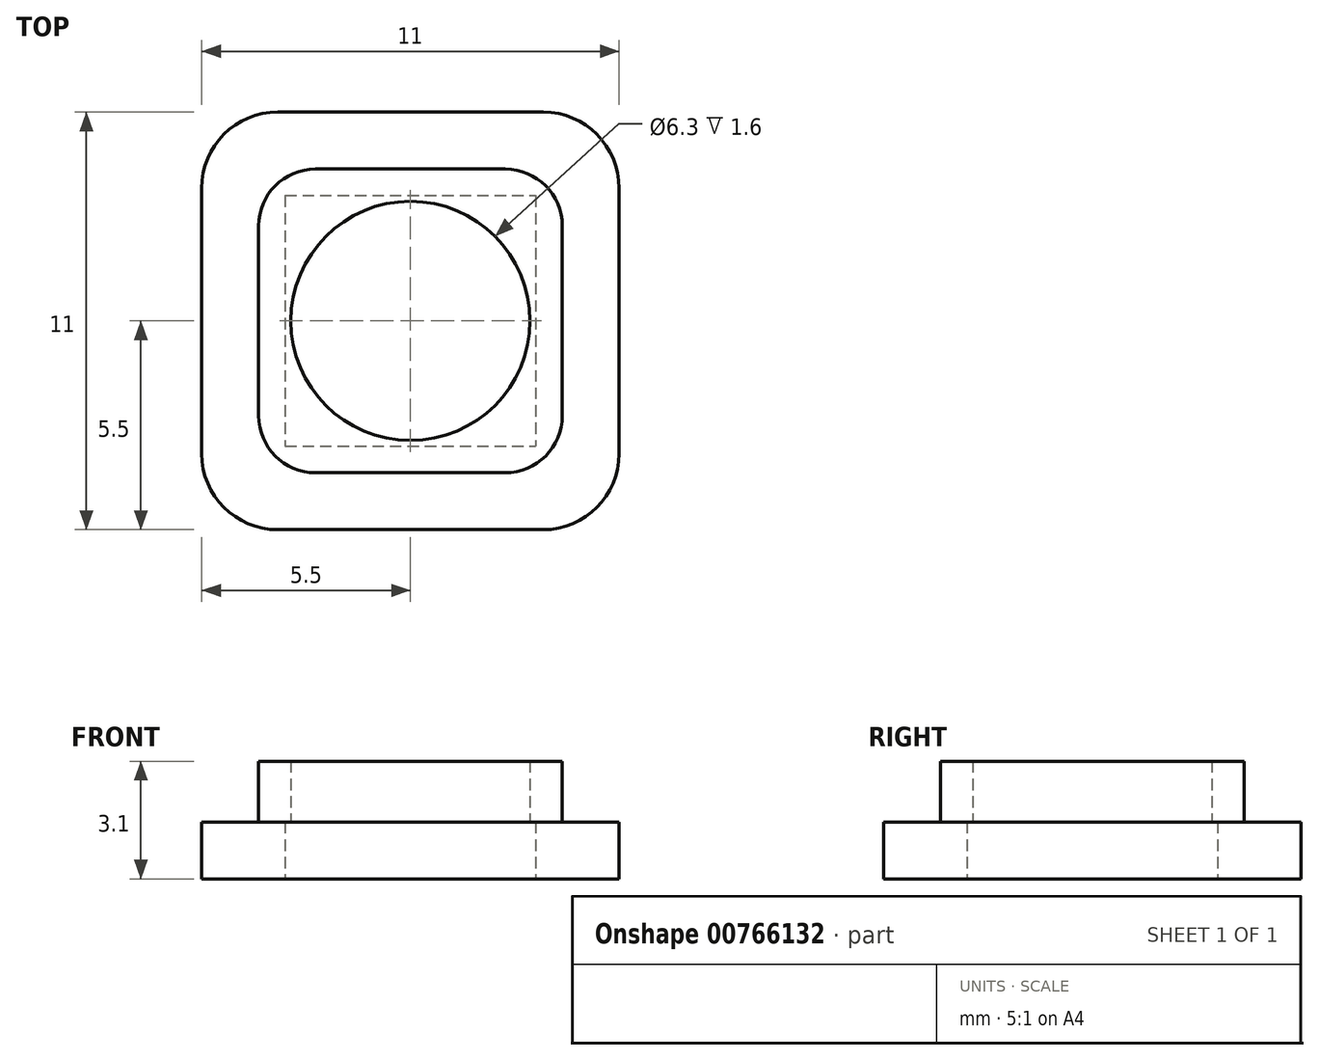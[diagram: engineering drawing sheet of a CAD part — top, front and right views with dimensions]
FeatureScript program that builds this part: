
annotation { "Feature Type Name" : "Feature", "Feature Type Description" : "" }
export const myFeature = defineFeature(function(context is Context, id is Id, definition is map)
    precondition{}
    {
        {
            var Q0;
            Q0=qCreatedBy(makeId("Top.planeOp"),FACE);
            var sketch = newSketch(context, id + "F0", { "sketchPlane" : qUnion([Q0])});
            skLineSegment(sketch, "E0.bottom", {"start": v(-3.5, 5.5) * mm, "end": v(3.5, 5.5) * mm});
            skLineSegment(sketch, "E0.top", {"start": v(-3.5, -5.5) * mm, "end": v(3.5, -5.5) * mm});
            skLineSegment(sketch, "E0.left", {"start": v(-5.5, 3.5) * mm, "end": v(-5.5, -3.5) * mm});
            skLineSegment(sketch, "E0.right", {"start": v(5.5, 3.5) * mm, "end": v(5.5, -3.5) * mm});
            skPoint(sketch, "E1", {"position": v(0, 5.5) * mm});
            skPoint(sketch, "E2", {"position": v(5.5, 0) * mm});
            skPoint(sketch, "E3", {"position": v(0, 0) * mm});
            skPoint(sketch, "E4", {"position": v(0, -5.5) * mm});
            skPoint(sketch, "E5", {"position": v(-5.5, 0) * mm});
            skLineSegment(sketch, "E6.bottom", {"start": v(-2.5, 4) * mm, "end": v(2.5, 4) * mm});
            skLineSegment(sketch, "E6.top", {"start": v(-2.5, -4) * mm, "end": v(2.5, -4) * mm});
            skLineSegment(sketch, "E6.left", {"start": v(-4, 2.5) * mm, "end": v(-4, -2.5) * mm});
            skLineSegment(sketch, "E6.right", {"start": v(4, 2.5) * mm, "end": v(4, -2.5) * mm});
            skPoint(sketch, "E7", {"position": v(4, 0) * mm});
            skPoint(sketch, "E8", {"position": v(0, 4) * mm});
            skPoint(sketch, "E9.visualSharp", {"position": v(5.5, 5.5) * mm});
            skArc(sketch, "E9.filletArc", {"start": v(5.5, 3.5) * mm, "mid": v(4.91, 4.91) * mm, "end": v(3.5, 5.5) * mm});
            skPoint(sketch, "E10.visualSharp", {"position": v(-5.5, 5.5) * mm});
            skArc(sketch, "E10.filletArc", {"start": v(-3.5, 5.5) * mm, "mid": v(-4.91, 4.91) * mm, "end": v(-5.5, 3.5) * mm});
            skPoint(sketch, "E11.visualSharp", {"position": v(-5.5, -5.5) * mm});
            skArc(sketch, "E11.filletArc", {"start": v(-5.5, -3.5) * mm, "mid": v(-4.91, -4.91) * mm, "end": v(-3.5, -5.5) * mm});
            skPoint(sketch, "E12.visualSharp", {"position": v(5.5, -5.5) * mm});
            skArc(sketch, "E12.filletArc", {"start": v(3.5, -5.5) * mm, "mid": v(4.91, -4.91) * mm, "end": v(5.5, -3.5) * mm});
            skPoint(sketch, "E13.visualSharp", {"position": v(-4, 4) * mm});
            skArc(sketch, "E13.filletArc", {"start": v(-2.5, 4) * mm, "mid": v(-3.56, 3.56) * mm, "end": v(-4, 2.5) * mm});
            skPoint(sketch, "E14.visualSharp", {"position": v(-4, -4) * mm});
            skArc(sketch, "E14.filletArc", {"start": v(-4, -2.5) * mm, "mid": v(-3.56, -3.56) * mm, "end": v(-2.5, -4) * mm});
            skPoint(sketch, "E15.visualSharp", {"position": v(4, -4) * mm});
            skArc(sketch, "E15.filletArc", {"start": v(2.5, -4) * mm, "mid": v(3.56, -3.56) * mm, "end": v(4, -2.5) * mm});
            skPoint(sketch, "E16.visualSharp", {"position": v(4, 4) * mm});
            skArc(sketch, "E16.filletArc", {"start": v(4, 2.5) * mm, "mid": v(3.56, 3.56) * mm, "end": v(2.5, 4) * mm});
            skCircle(sketch, "E17", {"center": v(0, 0) * mm, "radius": 3.15 * mm});
            skLineSegment(sketch, "E18.bottom", {"start": v(-3.3, 3.3) * mm, "end": v(3.3, 3.3) * mm});
            skLineSegment(sketch, "E18.top", {"start": v(-3.3, -3.3) * mm, "end": v(3.3, -3.3) * mm});
            skLineSegment(sketch, "E18.left", {"start": v(-3.3, 3.3) * mm, "end": v(-3.3, -3.3) * mm});
            skLineSegment(sketch, "E18.right", {"start": v(3.3, 3.3) * mm, "end": v(3.3, -3.3) * mm});
            skPoint(sketch, "E19", {"position": v(0, 3.3) * mm});
            skPoint(sketch, "E20", {"position": v(-3.3, 0) * mm});
            skSolve(sketch);
        }
        {
            var Q0;
            Q0=makeQuery(id+"F0.imprint","IMPRINT",FACE,{"disambiguationData":[TD([[makeQuery(id+"F0.imprint","IMPRINT",EDGE,{"derivedFrom":sQuery(id+"F0.wireOp",EDGE,"E0.bottom")}),-1.0]])]});
            var Q1;
            Q1=makeQuery(id+"F0.imprint","IMPRINT",FACE,{"disambiguationData":[TD([[makeQuery(id+"F0.imprint","IMPRINT",EDGE,{"derivedFrom":sQuery(id+"F0.wireOp",EDGE,"E6.bottom")}),-1.0]])]});
            var Q2;
            Q2=makeQuery(id+"F0.imprint","IMPRINT",FACE,{"disambiguationData":[TD([[makeQuery(id+"F0.imprint","IMPRINT",EDGE,{"derivedFrom":sQuery(id+"F0.wireOp",EDGE,"E17")}),-1.0]])]});
            var Q3;
            Q3=makeQuery(id+"F0.imprint","IMPRINT",FACE,{"disambiguationData":[TD([[makeQuery(id+"F0.imprint","IMPRINT",EDGE,{"derivedFrom":sQuery(id+"F0.wireOp",EDGE,"E17")}),1.0]])]});
            extrude(context, id + "F1", {"entities" : qUnion([Q0, Q1, Q2, Q3]), "depth" : 1.5 * mm, "offsetDistance" : 25 * mm});
        }
        {
            var Q0;
            Q0=makeQuery(id+"F0.imprint","IMPRINT",FACE,{"disambiguationData":[TD([[makeQuery(id+"F0.imprint","IMPRINT",EDGE,{"derivedFrom":sQuery(id+"F0.wireOp",EDGE,"E6.bottom")}),-1.0]])]});
            var Q1;
            Q1=makeQuery(id+"F0.imprint","IMPRINT",FACE,{"disambiguationData":[TD([[makeQuery(id+"F0.imprint","IMPRINT",EDGE,{"derivedFrom":sQuery(id+"F0.wireOp",EDGE,"E17")}),-1.0]])]});
            var Q2;
            Q2=makeQuery(id+"F0.imprint","IMPRINT",FACE,{"disambiguationData":[TD([[makeQuery(id+"F0.imprint","IMPRINT",EDGE,{"derivedFrom":sQuery(id+"F0.wireOp",EDGE,"E17")}),1.0]])]});
            extrude(context, id + "F2", {"entities" : qUnion([Q0, Q1, Q2]), "operationType" : NewBodyOperationType.ADD, "depth" : 3.1 * mm, "offsetDistance" : 25 * mm});
        }
        {
            var Q0;
            Q0=makeQuery(id+"F0.imprint","IMPRINT",FACE,{"disambiguationData":[TD([[makeQuery(id+"F0.imprint","IMPRINT",EDGE,{"derivedFrom":sQuery(id+"F0.wireOp",EDGE,"E17")}),1.0]])]});
            extrude(context, id + "F3", {"entities" : qUnion([Q0]), "operationType" : NewBodyOperationType.REMOVE, "endBound" : BoundingType.THROUGH_ALL, "depth" : 25 * mm, "offsetDistance" : 25 * mm});
        }
        {
            var Q0;
            Q0=makeQuery(id+"F0.imprint","IMPRINT",FACE,{"disambiguationData":[TD([[makeQuery(id+"F0.imprint","IMPRINT",EDGE,{"derivedFrom":sQuery(id+"F0.wireOp",EDGE,"E17")}),-1.0]])]});
            var Q1;
            Q1=makeQuery(id+"F0.imprint","IMPRINT",FACE,{"disambiguationData":[TD([[makeQuery(id+"F0.imprint","IMPRINT",EDGE,{"derivedFrom":sQuery(id+"F0.wireOp",EDGE,"E17")}),1.0]])]});
            extrude(context, id + "F4", {"entities" : qUnion([Q0, Q1]), "operationType" : NewBodyOperationType.REMOVE, "depth" : 1.5 * mm, "offsetDistance" : 25 * mm});
        }
    });
